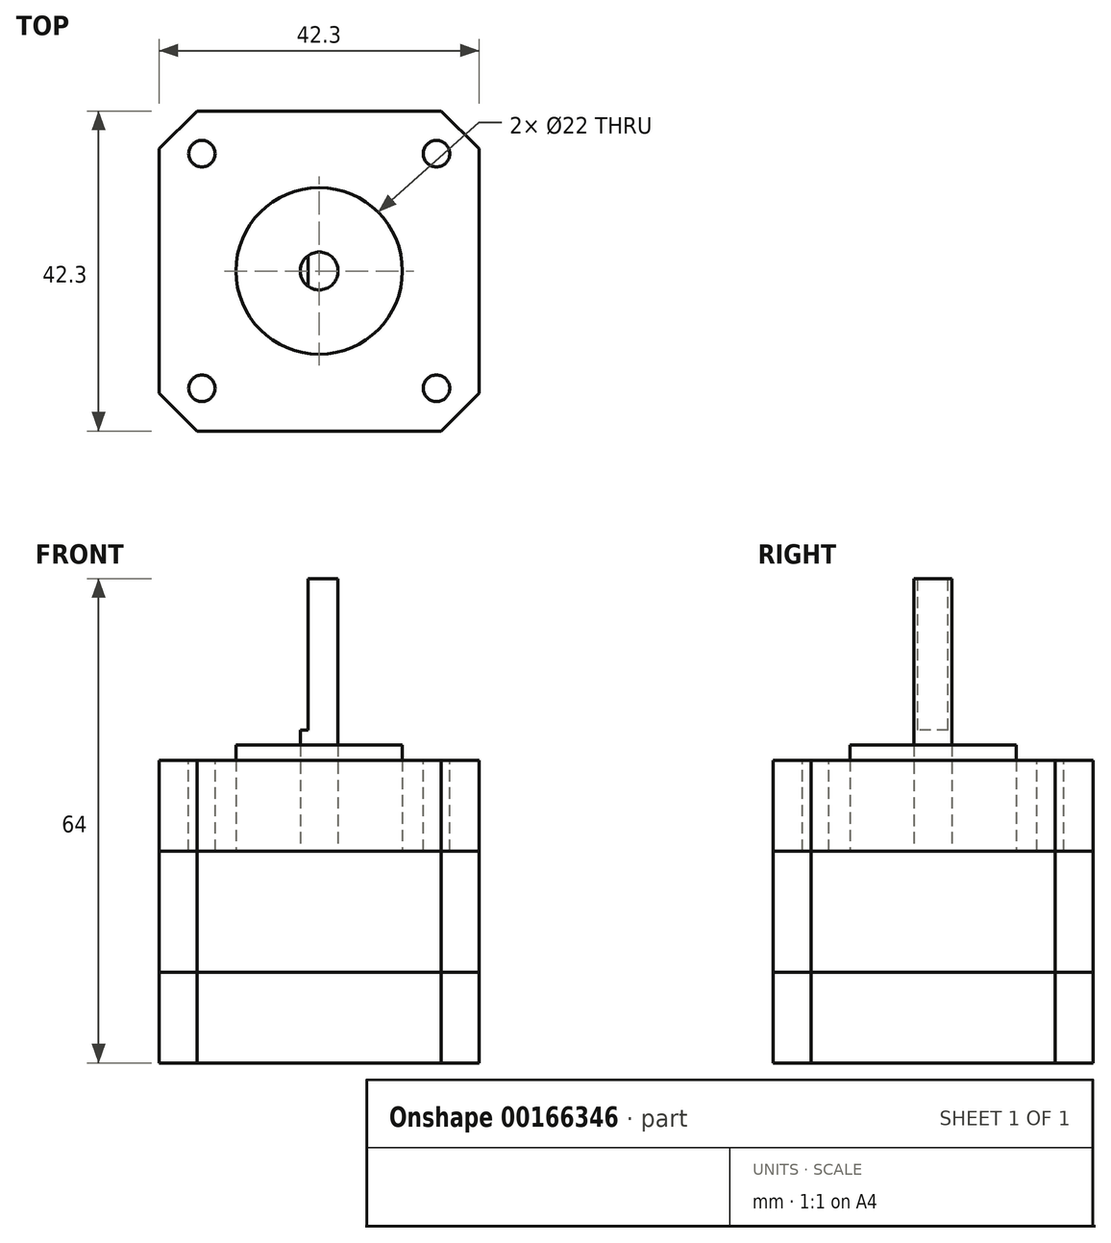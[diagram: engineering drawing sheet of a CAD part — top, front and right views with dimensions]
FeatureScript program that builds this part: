
annotation { "Feature Type Name" : "Feature", "Feature Type Description" : "" }
export const myFeature = defineFeature(function(context is Context, id is Id, definition is map)
    precondition{}
    {
        {
            var Q0;
            Q0=qCreatedBy(makeId("Top.planeOp"),FACE);
            var sketch = newSketch(context, id + "F0", { "sketchPlane" : qUnion([Q0])});
            skLineSegment(sketch, "E0.bottom", {"start": v(21.15, 21.15) * mm, "end": v(-21.15, 21.15) * mm});
            skLineSegment(sketch, "E0.top", {"start": v(21.15, -21.15) * mm, "end": v(-21.15, -21.15) * mm});
            skLineSegment(sketch, "E0.left", {"start": v(21.15, 21.15) * mm, "end": v(21.15, -21.15) * mm});
            skLineSegment(sketch, "E0.right", {"start": v(-21.15, 21.15) * mm, "end": v(-21.15, -21.15) * mm});
            skPoint(sketch, "E0.middle", {"position": v(0, 0) * mm});
            skSolve(sketch);
        }
        {
            var Q0;
            Q0 = qSketchRegion(id + "F0", true);
            extrude(context, id + "F1", {"entities" : qUnion([Q0]), "depth" : 12 * mm});
        }
        {
            var Q0;
            Q0=makeQuery(id+"F1.opExtrude","SWEPT_EDGE",EDGE,{"disambiguationData":[OSD([sQuery(id+"F0.wireOp",EDGE,"E0.top"),sQuery(id+"F0.wireOp",EDGE,"E0.left")])]});
            var Q1;
            Q1=makeQuery(id+"F1.opExtrude","SWEPT_EDGE",EDGE,{"disambiguationData":[OSD([sQuery(id+"F0.wireOp",EDGE,"E0.bottom"),sQuery(id+"F0.wireOp",EDGE,"E0.left")])]});
            var Q2;
            Q2=makeQuery(id+"F1.opExtrude","SWEPT_EDGE",EDGE,{"disambiguationData":[OSD([sQuery(id+"F0.wireOp",EDGE,"E0.top"),sQuery(id+"F0.wireOp",EDGE,"E0.right")])]});
            var Q3;
            Q3=makeQuery(id+"F1.opExtrude","SWEPT_EDGE",EDGE,{"disambiguationData":[OSD([sQuery(id+"F0.wireOp",EDGE,"E0.bottom"),sQuery(id+"F0.wireOp",EDGE,"E0.right")])]});
            chamfer(context, id + "F2", {"entities" : qUnion([Q0, Q1, Q2, Q3]), "width" : 5 * mm, "tangentPropagation" : true});
        }
        {
            var Q0;
            Q0=makeQuery(id+"F1.opExtrude","CAP_FACE",FACE,{"disambiguationData":[OSD([sQuery(id+"F0.wireOp",EDGE,"E0.bottom"),sQuery(id+"F0.wireOp",EDGE,"E0.top"),sQuery(id+"F0.wireOp",EDGE,"E0.left"),sQuery(id+"F0.wireOp",EDGE,"E0.right")])],"isStart":false});
            var sketch = newSketch(context, id + "F3", { "sketchPlane" : qUnion([Q0])});
            skLineSegment(sketch, "E1.bottom", {"start": v(21.15, 21.15) * mm, "end": v(-21.15, 21.15) * mm});
            skLineSegment(sketch, "E1.top", {"start": v(21.15, -21.15) * mm, "end": v(-21.15, -21.15) * mm});
            skLineSegment(sketch, "E1.left", {"start": v(21.15, 21.15) * mm, "end": v(21.15, -21.15) * mm});
            skLineSegment(sketch, "E1.right", {"start": v(-21.15, 21.15) * mm, "end": v(-21.15, -21.15) * mm});
            skPoint(sketch, "E1.middle", {"position": v(0, 0) * mm});
            skSolve(sketch);
        }
        {
            var Q0;
            Q0 = qSketchRegion(id + "F3", true);
            extrude(context, id + "F4", {"entities" : qUnion([Q0]), "depth" : 16 * mm});
        }
        {
            var Q0;
            Q0=makeQuery(id+"F4.opExtrude","SWEPT_EDGE",EDGE,{"disambiguationData":[OSD([sQuery(id+"F3.wireOp",EDGE,"E1.top"),sQuery(id+"F3.wireOp",EDGE,"E1.left")])]});
            var Q1;
            Q1=makeQuery(id+"F4.opExtrude","SWEPT_EDGE",EDGE,{"disambiguationData":[OSD([sQuery(id+"F3.wireOp",EDGE,"E1.bottom"),sQuery(id+"F3.wireOp",EDGE,"E1.left")])]});
            var Q2;
            Q2=makeQuery(id+"F4.opExtrude","SWEPT_EDGE",EDGE,{"disambiguationData":[OSD([sQuery(id+"F3.wireOp",EDGE,"E1.top"),sQuery(id+"F3.wireOp",EDGE,"E1.right")])]});
            var Q3;
            Q3=makeQuery(id+"F4.opExtrude","SWEPT_EDGE",EDGE,{"disambiguationData":[OSD([sQuery(id+"F3.wireOp",EDGE,"E1.bottom"),sQuery(id+"F3.wireOp",EDGE,"E1.right")])]});
            chamfer(context, id + "F5", {"entities" : qUnion([Q0, Q1, Q2, Q3]), "width" : 5 * mm, "tangentPropagation" : true});
        }
        {
            var Q0;
            Q0=makeQuery(id+"F4.opExtrude","CAP_FACE",FACE,{"disambiguationData":[OSD([sQuery(id+"F3.wireOp",EDGE,"E1.bottom"),sQuery(id+"F3.wireOp",EDGE,"E1.top"),sQuery(id+"F3.wireOp",EDGE,"E1.left"),sQuery(id+"F3.wireOp",EDGE,"E1.right")])],"isStart":false});
            var sketch = newSketch(context, id + "F6", { "sketchPlane" : qUnion([Q0])});
            skLineSegment(sketch, "E2.bottom", {"start": v(-21.15, 21.15) * mm, "end": v(21.15, 21.15) * mm});
            skLineSegment(sketch, "E2.top", {"start": v(-21.15, -21.15) * mm, "end": v(21.15, -21.15) * mm});
            skLineSegment(sketch, "E2.left", {"start": v(-21.15, 21.15) * mm, "end": v(-21.15, -21.15) * mm});
            skLineSegment(sketch, "E2.right", {"start": v(21.15, 21.15) * mm, "end": v(21.15, -21.15) * mm});
            skPoint(sketch, "E2.middle", {"position": v(0, 0) * mm});
            skSolve(sketch);
        }
        {
            var Q0;
            Q0 = qSketchRegion(id + "F6", true);
            extrude(context, id + "F7", {"entities" : qUnion([Q0]), "depth" : 12 * mm});
        }
        {
            var Q0;
            Q0=makeQuery(id+"F7.opExtrude","SWEPT_EDGE",EDGE,{"disambiguationData":[OSD([sQuery(id+"F6.wireOp",EDGE,"E2.top"),sQuery(id+"F6.wireOp",EDGE,"E2.right")])]});
            var Q1;
            Q1=makeQuery(id+"F7.opExtrude","SWEPT_EDGE",EDGE,{"disambiguationData":[OSD([sQuery(id+"F6.wireOp",EDGE,"E2.bottom"),sQuery(id+"F6.wireOp",EDGE,"E2.right")])]});
            var Q2;
            Q2=makeQuery(id+"F7.opExtrude","SWEPT_EDGE",EDGE,{"disambiguationData":[OSD([sQuery(id+"F6.wireOp",EDGE,"E2.bottom"),sQuery(id+"F6.wireOp",EDGE,"E2.left")])]});
            var Q3;
            Q3=makeQuery(id+"F7.opExtrude","SWEPT_EDGE",EDGE,{"disambiguationData":[OSD([sQuery(id+"F6.wireOp",EDGE,"E2.top"),sQuery(id+"F6.wireOp",EDGE,"E2.left")])]});
            chamfer(context, id + "F8", {"entities" : qUnion([Q0, Q1, Q2, Q3]), "width" : 5 * mm, "tangentPropagation" : true});
        }
        {
            var Q0;
            Q0=makeQuery(id+"F7.opExtrude","CAP_FACE",FACE,{"disambiguationData":[OSD([sQuery(id+"F6.wireOp",EDGE,"E2.bottom"),sQuery(id+"F6.wireOp",EDGE,"E2.top"),sQuery(id+"F6.wireOp",EDGE,"E2.left"),sQuery(id+"F6.wireOp",EDGE,"E2.right")])],"isStart":false});
            var sketch = newSketch(context, id + "F9", { "sketchPlane" : qUnion([Q0])});
            skCircle(sketch, "E3", {"center": v(0, 0) * mm, "radius": 11 * mm});
            skLineSegment(sketch, "E4.bottom", {"start": v(15.5, 15.5) * mm, "end": v(-15.5, 15.5) * mm});
            skLineSegment(sketch, "E4.top", {"start": v(15.5, -15.5) * mm, "end": v(-15.5, -15.5) * mm});
            skLineSegment(sketch, "E4.left", {"start": v(15.5, 15.5) * mm, "end": v(15.5, -15.5) * mm});
            skLineSegment(sketch, "E4.right", {"start": v(-15.5, 15.5) * mm, "end": v(-15.5, -15.5) * mm});
            skCircle(sketch, "E5", {"center": v(15.5, 15.5) * mm, "radius": 1.75 * mm});
            skCircle(sketch, "E6.1.0", {"center": v(-15.5, 15.5) * mm, "radius": 1.75 * mm});
            skCircle(sketch, "E6.2.0", {"center": v(-15.5, -15.5) * mm, "radius": 1.75 * mm});
            skCircle(sketch, "E6.3.0", {"center": v(15.5, -15.5) * mm, "radius": 1.75 * mm});
            skSolve(sketch);
        }
        {
            var Q0;
            {var subQ0=sQuery(id+"F9.wireOp",EDGE,"E4.left");var subQ1=sQuery(id+"F9.wireOp",EDGE,"E4.bottom");var subQ2=makeQuery(id+"F9.imprint","INTERSECT",VERTEX,{"derivedFrom":[subQ1,subQ0]});Q0=makeQuery(id+"F9.imprint","IMPRINT",FACE,{"disambiguationData":[TD([[makeQuery(id+"F9.imprint","IMPRINT",EDGE,{"disambiguationData":[TD([[subQ2,-1.0]])],"derivedFrom":subQ1}),1.0]])]});}
            var Q1;
            {var subQ0=sQuery(id+"F9.wireOp",EDGE,"E4.left");var subQ1=sQuery(id+"F9.wireOp",EDGE,"E4.bottom");var subQ2=makeQuery(id+"F9.imprint","INTERSECT",VERTEX,{"derivedFrom":[subQ1,subQ0]});Q1=makeQuery(id+"F9.imprint","IMPRINT",FACE,{"disambiguationData":[TD([[makeQuery(id+"F9.imprint","IMPRINT",EDGE,{"disambiguationData":[TD([[subQ2,-1.0]])],"derivedFrom":subQ1}),-1.0]])]});}
            var Q2;
            {var subQ0=sQuery(id+"F9.wireOp",EDGE,"E4.right");var subQ1=sQuery(id+"F9.wireOp",EDGE,"E4.bottom");var subQ2=makeQuery(id+"F9.imprint","INTERSECT",VERTEX,{"derivedFrom":[subQ1,subQ0]});Q2=makeQuery(id+"F9.imprint","IMPRINT",FACE,{"disambiguationData":[TD([[makeQuery(id+"F9.imprint","IMPRINT",EDGE,{"disambiguationData":[TD([[subQ2,1.0]])],"derivedFrom":subQ1}),1.0]])]});}
            var Q3;
            {var subQ0=sQuery(id+"F9.wireOp",EDGE,"E4.right");var subQ1=sQuery(id+"F9.wireOp",EDGE,"E4.bottom");var subQ2=makeQuery(id+"F9.imprint","INTERSECT",VERTEX,{"derivedFrom":[subQ1,subQ0]});Q3=makeQuery(id+"F9.imprint","IMPRINT",FACE,{"disambiguationData":[TD([[makeQuery(id+"F9.imprint","IMPRINT",EDGE,{"disambiguationData":[TD([[subQ2,1.0]])],"derivedFrom":subQ1}),-1.0]])]});}
            var Q4;
            {var subQ0=sQuery(id+"F9.wireOp",EDGE,"E4.left");var subQ1=sQuery(id+"F9.wireOp",EDGE,"E4.top");var subQ2=makeQuery(id+"F9.imprint","INTERSECT",VERTEX,{"derivedFrom":[subQ1,subQ0]});Q4=makeQuery(id+"F9.imprint","IMPRINT",FACE,{"disambiguationData":[TD([[makeQuery(id+"F9.imprint","IMPRINT",EDGE,{"disambiguationData":[TD([[subQ2,-1.0]])],"derivedFrom":subQ1}),-1.0]])]});}
            var Q5;
            {var subQ0=sQuery(id+"F9.wireOp",EDGE,"E4.left");var subQ1=sQuery(id+"F9.wireOp",EDGE,"E4.top");var subQ2=makeQuery(id+"F9.imprint","INTERSECT",VERTEX,{"derivedFrom":[subQ1,subQ0]});Q5=makeQuery(id+"F9.imprint","IMPRINT",FACE,{"disambiguationData":[TD([[makeQuery(id+"F9.imprint","IMPRINT",EDGE,{"disambiguationData":[TD([[subQ2,-1.0]])],"derivedFrom":subQ1}),1.0]])]});}
            var Q6;
            {var subQ0=sQuery(id+"F9.wireOp",EDGE,"E4.right");var subQ1=sQuery(id+"F9.wireOp",EDGE,"E4.top");var subQ2=makeQuery(id+"F9.imprint","INTERSECT",VERTEX,{"derivedFrom":[subQ1,subQ0]});Q6=makeQuery(id+"F9.imprint","IMPRINT",FACE,{"disambiguationData":[TD([[makeQuery(id+"F9.imprint","IMPRINT",EDGE,{"disambiguationData":[TD([[subQ2,1.0]])],"derivedFrom":subQ1}),-1.0]])]});}
            var Q7;
            {var subQ0=sQuery(id+"F9.wireOp",EDGE,"E4.right");var subQ1=sQuery(id+"F9.wireOp",EDGE,"E4.top");var subQ2=makeQuery(id+"F9.imprint","INTERSECT",VERTEX,{"derivedFrom":[subQ1,subQ0]});Q7=makeQuery(id+"F9.imprint","IMPRINT",FACE,{"disambiguationData":[TD([[makeQuery(id+"F9.imprint","IMPRINT",EDGE,{"disambiguationData":[TD([[subQ2,1.0]])],"derivedFrom":subQ1}),1.0]])]});}
            var Q8;
            Q8=makeQuery(id+"F9.imprint","IMPRINT",FACE,{"disambiguationData":[TD([[makeQuery(id+"F9.imprint","IMPRINT",EDGE,{"derivedFrom":sQuery(id+"F9.wireOp",EDGE,"E3")}),1.0]])]});
            extrude(context, id + "F10", {"entities" : qUnion([Q0, Q1, Q2, Q3, Q4, Q5, Q6, Q7, Q8]), "operationType" : NewBodyOperationType.REMOVE, "oppositeDirection" : true, "depth" : 12 * mm});
        }
        {
            var Q0;
            Q0=makeQuery(id+"F4.opExtrude","CAP_FACE",FACE,{"disambiguationData":[OSD([sQuery(id+"F3.wireOp",EDGE,"E1.bottom"),sQuery(id+"F3.wireOp",EDGE,"E1.top"),sQuery(id+"F3.wireOp",EDGE,"E1.left"),sQuery(id+"F3.wireOp",EDGE,"E1.right")])],"isStart":false});
            var sketch = newSketch(context, id + "F11", { "sketchPlane" : qUnion([Q0])});
            skCircle(sketch, "E7", {"center": v(0, 0) * mm, "radius": 11 * mm});
            skCircle(sketch, "E8", {"center": v(0, 0) * mm, "radius": 2.5 * mm});
            skSolve(sketch);
        }
        {
            var Q0;
            Q0 = qSketchRegion(id + "F11", true);
            extrude(context, id + "F12", {"entities" : qUnion([Q0]), "depth" : 14 * mm});
        }
        {
            var Q0;
            Q0=makeQuery(id+"F4.opExtrude","CAP_FACE",FACE,{"disambiguationData":[OSD([sQuery(id+"F3.wireOp",EDGE,"E1.bottom"),sQuery(id+"F3.wireOp",EDGE,"E1.top"),sQuery(id+"F3.wireOp",EDGE,"E1.left"),sQuery(id+"F3.wireOp",EDGE,"E1.right")])],"isStart":false});
            var sketch = newSketch(context, id + "F13", { "sketchPlane" : qUnion([Q0])});
            skCircle(sketch, "E9", {"center": v(0, 0) * mm, "radius": 2.5 * mm});
            skSolve(sketch);
        }
        {
            var Q0;
            Q0 = qSketchRegion(id + "F13", true);
            extrude(context, id + "F14", {"entities" : qUnion([Q0]), "depth" : 36 * mm});
        }
        {
            var Q0;
            Q0=makeQuery(id+"F14.opExtrude","CAP_FACE",FACE,{"disambiguationData":[OSD([sQuery(id+"F13.wireOp",EDGE,"E9")])],"isStart":false});
            var sketch = newSketch(context, id + "F15", { "sketchPlane" : qUnion([Q0])});
            skLineSegment(sketch, "E10", {"start": v(0, 0) * mm, "end": v(-1.5, 0) * mm});
            skLineSegment(sketch, "E11", {"start": v(-1.5, 0) * mm, "end": v(-1.5, -2) * mm});
            skLineSegment(sketch, "E12", {"start": v(-1.5, -2) * mm, "end": v(-1.5, 2) * mm});
            skCircle(sketch, "E13", {"center": v(0, 0) * mm, "radius": 2.5 * mm});
            skSolve(sketch);
        }
        {
            var Q0;
            {var subQ0=sQuery(id+"F15.wireOp",EDGE,"E12");var subQ1=makeQuery(id+"F15.imprint","IMPRINT",VERTEX,{"derivedFrom":subQ0});Q0=makeQuery(id+"F15.imprint","IMPRINT",FACE,{"disambiguationData":[TD([[makeQuery(id+"F15.imprint","IMPRINT",EDGE,{"disambiguationData":[TD([[subQ1,1.0]])],"derivedFrom":subQ0}),1.0]])]});}
            extrude(context, id + "F16", {"entities" : qUnion([Q0]), "operationType" : NewBodyOperationType.REMOVE, "oppositeDirection" : true, "depth" : 20 * mm});
        }
    });
